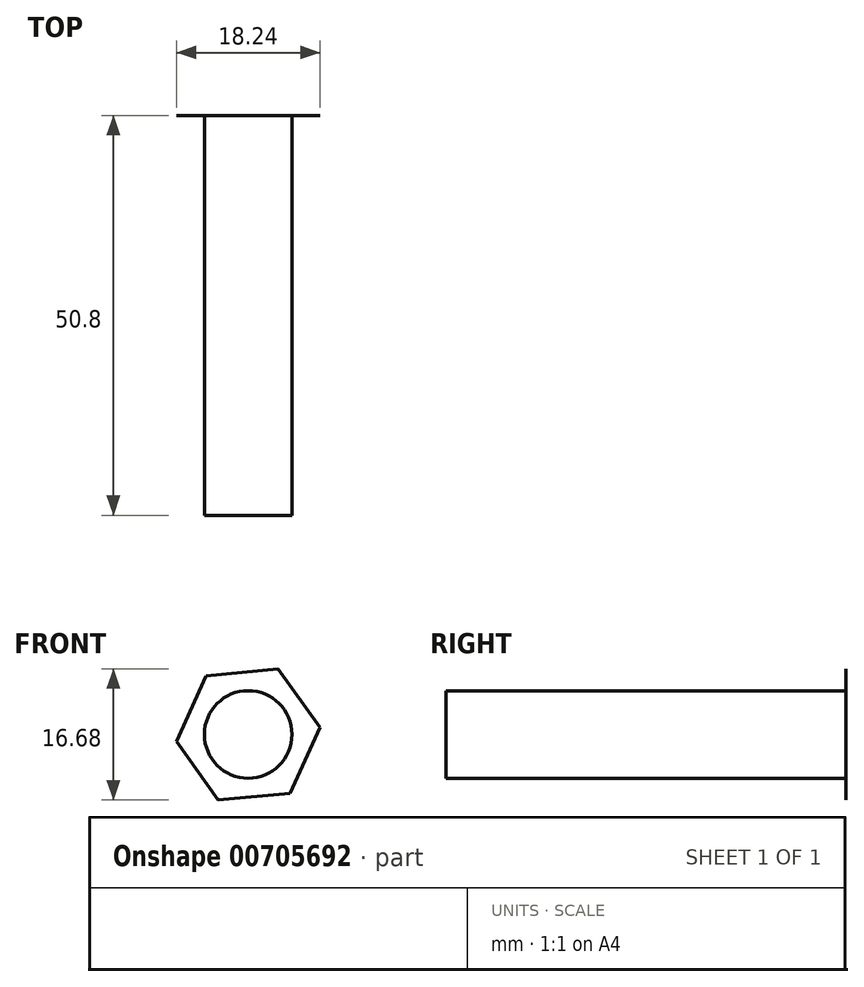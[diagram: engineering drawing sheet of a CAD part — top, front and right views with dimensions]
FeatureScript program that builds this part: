
annotation { "Feature Type Name" : "Feature", "Feature Type Description" : "" }
export const myFeature = defineFeature(function(context is Context, id is Id, definition is map)
    precondition{}
    {
        {
            var Q0;
            Q0=qCreatedBy(makeId("Front.planeOp"),FACE);
            var sketch = newSketch(context, id + "F0", { "sketchPlane" : qUnion([Q0])});
            skCircle(sketch, "E0.cCircle", {"center": v(0, 0) * mm, "radius": 7.94 * mm, "construction": true});
            skLineSegment(sketch, "E0.0", {"start": v(3.8, 8.34) * mm, "end": v(9.12, 0.88) * mm});
            skLineSegment(sketch, "E0.1", {"start": v(9.12, 0.88) * mm, "end": v(5.33, -7.46) * mm});
            skLineSegment(sketch, "E0.2", {"start": v(5.33, -7.46) * mm, "end": v(-3.8, -8.34) * mm});
            skLineSegment(sketch, "E0.3", {"start": v(-3.8, -8.34) * mm, "end": v(-9.12, -0.88) * mm});
            skLineSegment(sketch, "E0.4", {"start": v(-9.12, -0.88) * mm, "end": v(-5.33, 7.46) * mm});
            skLineSegment(sketch, "E0.5", {"start": v(-5.33, 7.46) * mm, "end": v(3.8, 8.34) * mm});
            skPoint(sketch, "E0.0.midPoint", {"position": v(6.46, 4.61) * mm});
            skSolve(sketch);
        }
        {
            var Q0;
            Q0 = qSketchRegion(id + "F0", true);
            extrude(context, id + "F1", {"entities" : qUnion([Q0]), "depth" : 9 / 812.8 * mm, "offsetDistance" : 25.4 * mm});
        }
        {
            var Q0;
            Q0=qCreatedBy(makeId("Front.planeOp"),FACE);
            var sketch = newSketch(context, id + "F2", { "sketchPlane" : qUnion([Q0])});
            skCircle(sketch, "E1", {"center": v(0, 0) * mm, "radius": 5.56 * mm});
            skSolve(sketch);
        }
        {
            var Q0;
            Q0 = qSketchRegion(id + "F2", true);
            extrude(context, id + "F3", {"entities" : qUnion([Q0]), "operationType" : NewBodyOperationType.ADD, "depth" : 50.8 * mm, "offsetDistance" : 25.4 * mm});
        }
    });
